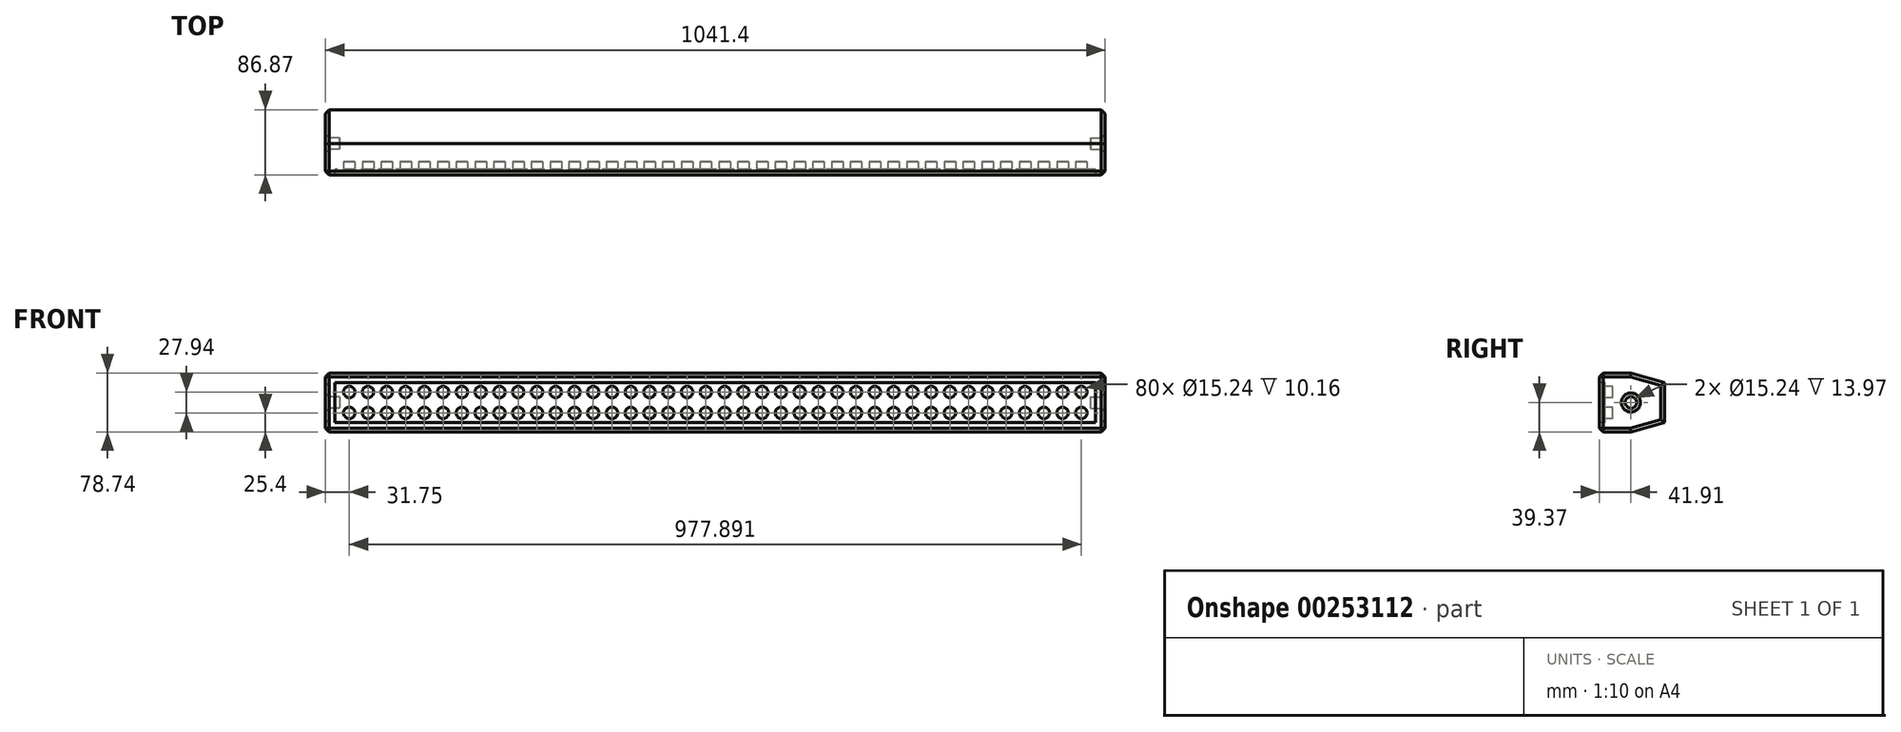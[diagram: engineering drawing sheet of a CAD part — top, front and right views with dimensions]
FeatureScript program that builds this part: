
annotation { "Feature Type Name" : "Feature", "Feature Type Description" : "" }
export const myFeature = defineFeature(function(context is Context, id is Id, definition is map)
    precondition{}
    {
        {
            var Q0;
            Q0=qCreatedBy(makeId("Right.planeOp"),FACE);
            var sketch = newSketch(context, id + "F0", { "sketchPlane" : qUnion([Q0])});
            skLineSegment(sketch, "E0", {"start": v(0, 0) * mm, "end": v(35.11, 0) * mm, "construction": true});
            skLineSegment(sketch, "E1", {"start": v(0, 39.37) * mm, "end": v(41.91, 39.37) * mm});
            skLineSegment(sketch, "E2", {"start": v(0, 39.37) * mm, "end": v(0, 0) * mm});
            skLineSegment(sketch, "E3.MirrorCS", {"start": v(0, -39.37) * mm, "end": v(41.91, -39.37) * mm});
            skLineSegment(sketch, "E4.MirrorCS", {"start": v(0, -39.37) * mm, "end": v(0, 0) * mm});
            skLineSegment(sketch, "E5", {"start": v(41.9, 39.37) * mm, "end": v(86.87, 26.67) * mm});
            skLineSegment(sketch, "E6", {"start": v(86.87, 26.67) * mm, "end": v(86.87, 0) * mm});
            skLineSegment(sketch, "E7.MirrorCS", {"start": v(-41.9, 39.37) * mm, "end": v(-86.87, 26.67) * mm});
            skLineSegment(sketch, "E8.MirrorCS", {"start": v(41.9, -39.37) * mm, "end": v(86.87, -26.67) * mm});
            skLineSegment(sketch, "E9.MirrorCS", {"start": v(86.87, -26.67) * mm, "end": v(86.87, 0) * mm});
            skSolve(sketch);
        }
        {
            var Q0;
            Q0 = qSketchRegion(id + "F0", true);
            extrude(context, id + "F1", {"entities" : qUnion([Q0]), "endBound" : BoundingType.SYMMETRIC, "depth" : 1041.4 * mm});
        }
        {
            var Q0;
            Q0=makeQuery(id+"F1.opExtrude","SWEPT_FACE",FACE,{"disambiguationData":[OSD([sQuery(id+"F0.wireOp",EDGE,"E2"),sQuery(id+"F0.wireOp",EDGE,"E4.MirrorCS")])]});
            var sketch = newSketch(context, id + "F2", { "sketchPlane" : qUnion([Q0])});
            skLineSegment(sketch, "E10.bottom", {"start": v(508, -26.67) * mm, "end": v(-508, -26.67) * mm});
            skLineSegment(sketch, "E10.top", {"start": v(508, 26.67) * mm, "end": v(-508, 26.67) * mm});
            skLineSegment(sketch, "E10.left", {"start": v(508, -26.67) * mm, "end": v(508, 26.67) * mm});
            skLineSegment(sketch, "E10.right", {"start": v(-508, -26.67) * mm, "end": v(-508, 26.67) * mm});
            skPoint(sketch, "E10.middle", {"position": v(0, 0) * mm});
            skSolve(sketch);
        }
        {
            var Q0;
            Q0 = qSketchRegion(id + "F2", true);
            extrude(context, id + "F3", {"entities" : qUnion([Q0]), "operationType" : NewBodyOperationType.REMOVE, "oppositeDirection" : true, "depth" : 7.62 * mm});
        }
        {
            var Q0;
            Q0=makeQuery(id+"F3.boolean.opBoolean","COPY",FACE,{"derivedFrom":makeQuery(id+"F3.opExtrude","CAP_FACE",FACE,{"disambiguationData":[OSD([sQuery(id+"F2.wireOp",EDGE,"E10.bottom"),sQuery(id+"F2.wireOp",EDGE,"E10.top"),sQuery(id+"F2.wireOp",EDGE,"E10.left"),sQuery(id+"F2.wireOp",EDGE,"E10.right")])],"isStart":false})});
            var sketch = newSketch(context, id + "F4", { "sketchPlane" : qUnion([Q0])});
            skCircle(sketch, "E11", {"center": v(-488.95, 13.97) * mm, "radius": 7.62 * mm});
            skLineSegment(sketch, "E12", {"start": v(0, 0) * mm, "end": v(-922.25, 0) * mm, "construction": true});
            skCircle(sketch, "E13.1.0.0", {"center": v(-463.88, 13.97) * mm, "radius": 7.62 * mm});
            skCircle(sketch, "E13.2.0.0", {"center": v(-438.8, 13.97) * mm, "radius": 7.62 * mm});
            skCircle(sketch, "E13.3.0.0", {"center": v(-413.73, 13.97) * mm, "radius": 7.62 * mm});
            skCircle(sketch, "E13.4.0.0", {"center": v(-388.65, 13.97) * mm, "radius": 7.62 * mm});
            skCircle(sketch, "E13.5.0.0", {"center": v(-363.58, 13.97) * mm, "radius": 7.62 * mm});
            skCircle(sketch, "E13.6.0.0", {"center": v(-338.5, 13.97) * mm, "radius": 7.62 * mm});
            skCircle(sketch, "E13.7.0.0", {"center": v(-313.43, 13.97) * mm, "radius": 7.62 * mm});
            skCircle(sketch, "E13.8.0.0", {"center": v(-288.36, 13.97) * mm, "radius": 7.62 * mm});
            skCircle(sketch, "E13.9.0.0", {"center": v(-263.28, 13.97) * mm, "radius": 7.62 * mm});
            skCircle(sketch, "E13.10.0.0", {"center": v(-238.2, 13.97) * mm, "radius": 7.62 * mm});
            skCircle(sketch, "E13.11.0.0", {"center": v(-213.13, 13.97) * mm, "radius": 7.62 * mm});
            skCircle(sketch, "E13.12.0.0", {"center": v(-188.06, 13.97) * mm, "radius": 7.62 * mm});
            skCircle(sketch, "E13.13.0.0", {"center": v(-162.99, 13.97) * mm, "radius": 7.62 * mm});
            skCircle(sketch, "E13.14.0.0", {"center": v(-137.91, 13.97) * mm, "radius": 7.62 * mm});
            skCircle(sketch, "E13.15.0.0", {"center": v(-112.84, 13.97) * mm, "radius": 7.62 * mm});
            skCircle(sketch, "E13.16.0.0", {"center": v(-87.76, 13.97) * mm, "radius": 7.62 * mm});
            skCircle(sketch, "E13.17.0.0", {"center": v(-62.7, 13.97) * mm, "radius": 7.62 * mm});
            skCircle(sketch, "E13.18.0.0", {"center": v(-37.62, 13.97) * mm, "radius": 7.62 * mm});
            skCircle(sketch, "E13.19.0.0", {"center": v(-12.54, 13.97) * mm, "radius": 7.62 * mm});
            skCircle(sketch, "E13.20.0.0", {"center": v(12.53, 13.97) * mm, "radius": 7.62 * mm});
            skCircle(sketch, "E13.21.0.0", {"center": v(37.6, 13.97) * mm, "radius": 7.62 * mm});
            skCircle(sketch, "E13.22.0.0", {"center": v(62.68, 13.97) * mm, "radius": 7.62 * mm});
            skCircle(sketch, "E13.23.0.0", {"center": v(87.75, 13.97) * mm, "radius": 7.62 * mm});
            skCircle(sketch, "E13.24.0.0", {"center": v(112.83, 13.97) * mm, "radius": 7.62 * mm});
            skCircle(sketch, "E13.25.0.0", {"center": v(137.9, 13.97) * mm, "radius": 7.62 * mm});
            skCircle(sketch, "E13.26.0.0", {"center": v(162.98, 13.97) * mm, "radius": 7.62 * mm});
            skCircle(sketch, "E13.27.0.0", {"center": v(188.05, 13.97) * mm, "radius": 7.62 * mm});
            skCircle(sketch, "E13.28.0.0", {"center": v(213.13, 13.97) * mm, "radius": 7.62 * mm});
            skCircle(sketch, "E13.29.0.0", {"center": v(238.2, 13.97) * mm, "radius": 7.62 * mm});
            skCircle(sketch, "E13.30.0.0", {"center": v(263.27, 13.97) * mm, "radius": 7.62 * mm});
            skCircle(sketch, "E13.31.0.0", {"center": v(288.35, 13.97) * mm, "radius": 7.62 * mm});
            skCircle(sketch, "E13.32.0.0", {"center": v(313.42, 13.97) * mm, "radius": 7.62 * mm});
            skCircle(sketch, "E13.33.0.0", {"center": v(338.5, 13.97) * mm, "radius": 7.62 * mm});
            skCircle(sketch, "E13.34.0.0", {"center": v(363.57, 13.97) * mm, "radius": 7.62 * mm});
            skCircle(sketch, "E13.35.0.0", {"center": v(388.64, 13.97) * mm, "radius": 7.62 * mm});
            skCircle(sketch, "E13.36.0.0", {"center": v(413.72, 13.97) * mm, "radius": 7.62 * mm});
            skCircle(sketch, "E13.37.0.0", {"center": v(438.8, 13.97) * mm, "radius": 7.62 * mm});
            skCircle(sketch, "E13.38.0.0", {"center": v(463.87, 13.97) * mm, "radius": 7.62 * mm});
            skCircle(sketch, "E13.39.0.0", {"center": v(488.94, 13.97) * mm, "radius": 7.62 * mm});
            skLineSegment(sketch, "E13.direction1", {"start": v(-488.95, 13.97) * mm, "end": v(-463.88, 13.97) * mm, "construction": true});
            skCircle(sketch, "E14.MirrorC", {"center": v(488.94, -13.97) * mm, "radius": 7.62 * mm});
            skCircle(sketch, "E15.MirrorC", {"center": v(-413.73, -13.97) * mm, "radius": 7.62 * mm});
            skCircle(sketch, "E16.MirrorC", {"center": v(-313.43, -13.97) * mm, "radius": 7.62 * mm});
            skCircle(sketch, "E17.MirrorC", {"center": v(12.53, -13.97) * mm, "radius": 7.62 * mm});
            skCircle(sketch, "E18.MirrorC", {"center": v(-37.62, -13.97) * mm, "radius": 7.62 * mm});
            skCircle(sketch, "E19.MirrorC", {"center": v(-87.76, -13.97) * mm, "radius": 7.62 * mm});
            skCircle(sketch, "E20.MirrorC", {"center": v(-388.65, -13.97) * mm, "radius": 7.62 * mm});
            skCircle(sketch, "E21.MirrorC", {"center": v(413.72, -13.97) * mm, "radius": 7.62 * mm});
            skCircle(sketch, "E22.MirrorC", {"center": v(363.57, -13.97) * mm, "radius": 7.62 * mm});
            skCircle(sketch, "E23.MirrorC", {"center": v(313.42, -13.97) * mm, "radius": 7.62 * mm});
            skCircle(sketch, "E24.MirrorC", {"center": v(-288.36, -13.97) * mm, "radius": 7.62 * mm});
            skCircle(sketch, "E25.MirrorC", {"center": v(-488.95, -13.97) * mm, "radius": 7.62 * mm});
            skCircle(sketch, "E26.MirrorC", {"center": v(238.2, -13.97) * mm, "radius": 7.62 * mm});
            skCircle(sketch, "E27.MirrorC", {"center": v(162.98, -13.97) * mm, "radius": 7.62 * mm});
            skCircle(sketch, "E28.MirrorC", {"center": v(62.68, -13.97) * mm, "radius": 7.62 * mm});
            skCircle(sketch, "E29.MirrorC", {"center": v(-363.58, -13.97) * mm, "radius": 7.62 * mm});
            skCircle(sketch, "E30.MirrorC", {"center": v(112.83, -13.97) * mm, "radius": 7.62 * mm});
            skCircle(sketch, "E31.MirrorC", {"center": v(-263.28, -13.97) * mm, "radius": 7.62 * mm});
            skCircle(sketch, "E32.MirrorC", {"center": v(-188.06, -13.97) * mm, "radius": 7.62 * mm});
            skLineSegment(sketch, "E33.MirrorCS", {"start": v(-488.95, -13.97) * mm, "end": v(-463.88, -13.97) * mm, "construction": true});
            skCircle(sketch, "E34.MirrorC", {"center": v(463.87, -13.97) * mm, "radius": 7.62 * mm});
            skCircle(sketch, "E35.MirrorC", {"center": v(-238.2, -13.97) * mm, "radius": 7.62 * mm});
            skCircle(sketch, "E36.MirrorC", {"center": v(-463.88, -13.97) * mm, "radius": 7.62 * mm});
            skCircle(sketch, "E37.MirrorC", {"center": v(37.6, -13.97) * mm, "radius": 7.62 * mm});
            skCircle(sketch, "E38.MirrorC", {"center": v(-162.99, -13.97) * mm, "radius": 7.62 * mm});
            skCircle(sketch, "E39.MirrorC", {"center": v(-62.7, -13.97) * mm, "radius": 7.62 * mm});
            skCircle(sketch, "E40.MirrorC", {"center": v(-112.84, -13.97) * mm, "radius": 7.62 * mm});
            skCircle(sketch, "E41.MirrorC", {"center": v(-12.54, -13.97) * mm, "radius": 7.62 * mm});
            skCircle(sketch, "E42.MirrorC", {"center": v(438.8, -13.97) * mm, "radius": 7.62 * mm});
            skCircle(sketch, "E43.MirrorC", {"center": v(388.64, -13.97) * mm, "radius": 7.62 * mm});
            skCircle(sketch, "E44.MirrorC", {"center": v(338.5, -13.97) * mm, "radius": 7.62 * mm});
            skCircle(sketch, "E45.MirrorC", {"center": v(288.35, -13.97) * mm, "radius": 7.62 * mm});
            skCircle(sketch, "E46.MirrorC", {"center": v(213.13, -13.97) * mm, "radius": 7.62 * mm});
            skCircle(sketch, "E47.MirrorC", {"center": v(263.27, -13.97) * mm, "radius": 7.62 * mm});
            skCircle(sketch, "E48.MirrorC", {"center": v(-213.13, -13.97) * mm, "radius": 7.62 * mm});
            skCircle(sketch, "E49.MirrorC", {"center": v(-438.8, -13.97) * mm, "radius": 7.62 * mm});
            skCircle(sketch, "E50.MirrorC", {"center": v(-137.91, -13.97) * mm, "radius": 7.62 * mm});
            skCircle(sketch, "E51.MirrorC", {"center": v(-338.5, -13.97) * mm, "radius": 7.62 * mm});
            skCircle(sketch, "E52.MirrorC", {"center": v(137.9, -13.97) * mm, "radius": 7.62 * mm});
            skCircle(sketch, "E53.MirrorC", {"center": v(87.75, -13.97) * mm, "radius": 7.62 * mm});
            skCircle(sketch, "E54.MirrorC", {"center": v(188.05, -13.97) * mm, "radius": 7.62 * mm});
            skSolve(sketch);
        }
        {
            var Q0;
            Q0 = qSketchRegion(id + "F4", true);
            extrude(context, id + "F5", {"entities" : qUnion([Q0]), "operationType" : NewBodyOperationType.REMOVE, "oppositeDirection" : true, "depth" : 10.16 * mm});
        }
        {
            var Q0;
            Q0=makeQuery(id+"F1.opExtrude","CAP_FACE",FACE,{"disambiguationData":[OSD([sQuery(id+"F0.wireOp",EDGE,"E1"),sQuery(id+"F0.wireOp",EDGE,"E2"),sQuery(id+"F0.wireOp",EDGE,"E3.MirrorCS"),sQuery(id+"F0.wireOp",EDGE,"E4.MirrorCS"),sQuery(id+"F0.wireOp",EDGE,"a03aa2aa-5a6f-4576-b362-bd34c7c2a79d.trimOffspring")])],"isStart":false});
            var sketch = newSketch(context, id + "F6", { "sketchPlane" : qUnion([Q0])});
            skCircle(sketch, "E55", {"center": v(41.91, 0) * mm, "radius": 7.62 * mm});
            skLineSegment(sketch, "E56", {"start": v(41.91, 39.37) * mm, "end": v(41.91, -39.37) * mm, "construction": true});
            skSolve(sketch);
        }
        {
            var Q0;
            Q0 = qSketchRegion(id + "F6", true);
            extrude(context, id + "F7", {"entities" : qUnion([Q0]), "operationType" : NewBodyOperationType.REMOVE, "oppositeDirection" : true, "depth" : 19.05 * mm});
        }
        {
            var Q0;
            Q0=makeQuery(id+"F1.opExtrude","CAP_FACE",FACE,{"disambiguationData":[OSD([sQuery(id+"F0.wireOp",EDGE,"E1"),sQuery(id+"F0.wireOp",EDGE,"E2"),sQuery(id+"F0.wireOp",EDGE,"E3.MirrorCS"),sQuery(id+"F0.wireOp",EDGE,"E4.MirrorCS"),sQuery(id+"F0.wireOp",EDGE,"a03aa2aa-5a6f-4576-b362-bd34c7c2a79d.trimOffspring")])],"isStart":true});
            var sketch = newSketch(context, id + "F8", { "sketchPlane" : qUnion([Q0])});
            skCircle(sketch, "E57", {"center": v(-41.91, 0) * mm, "radius": 7.62 * mm});
            skLineSegment(sketch, "E58", {"start": v(-41.91, 39.37) * mm, "end": v(-41.91, -39.37) * mm, "construction": true});
            skSolve(sketch);
        }
        {
            var Q0;
            Q0 = qSketchRegion(id + "F8", true);
            extrude(context, id + "F9", {"entities" : qUnion([Q0]), "operationType" : NewBodyOperationType.REMOVE, "oppositeDirection" : true, "depth" : 19.05 * mm});
        }
        {
            var Q0;
            Q0=makeQuery(id+"F1.opExtrude","CAP_FACE",FACE,{"disambiguationData":[OSD([sQuery(id+"F0.wireOp",EDGE,"E1"),sQuery(id+"F0.wireOp",EDGE,"E2"),sQuery(id+"F0.wireOp",EDGE,"E3.MirrorCS"),sQuery(id+"F0.wireOp",EDGE,"E4.MirrorCS"),sQuery(id+"F0.wireOp",EDGE,"a03aa2aa-5a6f-4576-b362-bd34c7c2a79d.trimOffspring")])],"isStart":true});
            var Q1;
            Q1=makeQuery(id+"F1.opExtrude","CAP_FACE",FACE,{"disambiguationData":[OSD([sQuery(id+"F0.wireOp",EDGE,"E1"),sQuery(id+"F0.wireOp",EDGE,"E2"),sQuery(id+"F0.wireOp",EDGE,"E3.MirrorCS"),sQuery(id+"F0.wireOp",EDGE,"E4.MirrorCS"),sQuery(id+"F0.wireOp",EDGE,"a03aa2aa-5a6f-4576-b362-bd34c7c2a79d.trimOffspring")])],"isStart":false});
            var Q2;
            Q2=makeQuery(id+"F1.opExtrude","SWEPT_EDGE",EDGE,{"disambiguationData":[OSD([sQuery(id+"F0.wireOp",EDGE,"E1"),sQuery(id+"F0.wireOp",EDGE,"E2")])]});
            var Q3;
            Q3=makeQuery(id+"F1.opExtrude","SWEPT_EDGE",EDGE,{"disambiguationData":[OSD([sQuery(id+"F0.wireOp",EDGE,"E3.MirrorCS"),sQuery(id+"F0.wireOp",EDGE,"E4.MirrorCS")])]});
            chamfer(context, id + "F10", {"entities" : qUnion([Q0, Q1, Q2, Q3]), "width" : 5.08 * mm, "tangentPropagation" : true});
        }
    });
